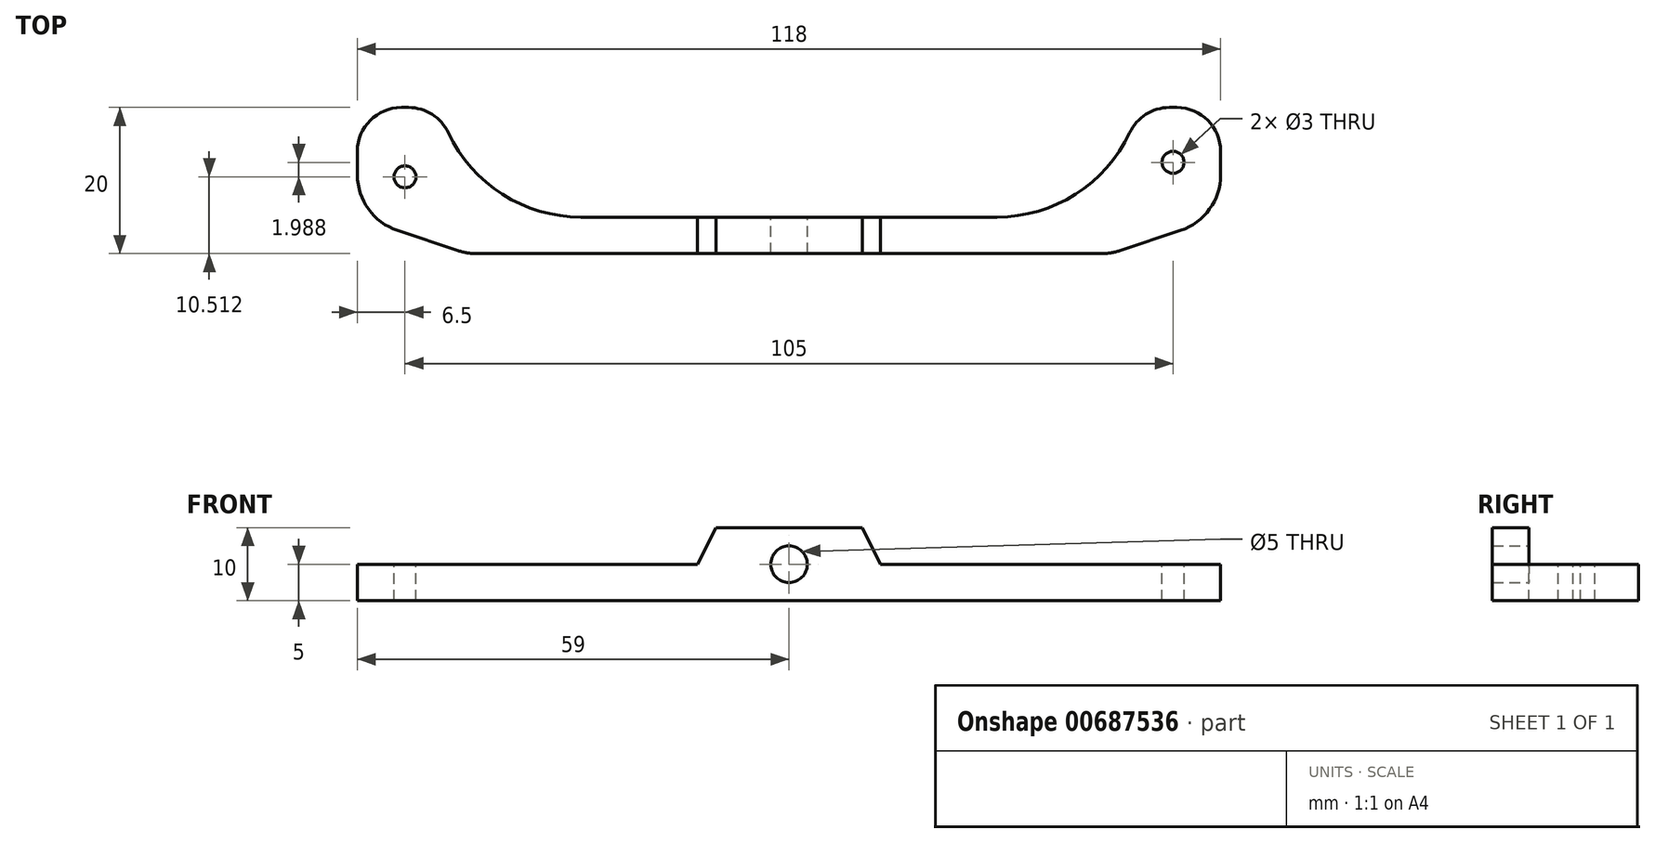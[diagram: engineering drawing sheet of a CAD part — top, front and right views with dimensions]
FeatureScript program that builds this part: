
annotation { "Feature Type Name" : "Feature", "Feature Type Description" : "" }
export const myFeature = defineFeature(function(context is Context, id is Id, definition is map)
    precondition{}
    {
        {
            var Q0;
            Q0=qCreatedBy(makeId("Top.planeOp"),FACE);
            var sketch = newSketch(context, id + "F0", { "sketchPlane" : qUnion([Q0])});
            skLineSegment(sketch, "E0", {"start": v(0, 0) * mm, "end": v(59, 0) * mm});
            skLineSegment(sketch, "E1", {"start": v(59, 0) * mm, "end": v(59, 20) * mm});
            skLineSegment(sketch, "E2", {"start": v(59, 20) * mm, "end": v(46, 20) * mm});
            skLineSegment(sketch, "E3", {"start": v(46, 20) * mm, "end": v(46, 5) * mm});
            skLineSegment(sketch, "E4", {"start": v(46, 5) * mm, "end": v(0, 5) * mm});
            skLineSegment(sketch, "E5", {"start": v(0, 5) * mm, "end": v(0, 0) * mm});
            skLineSegment(sketch, "E6.MirrorCS", {"start": v(-59, 20) * mm, "end": v(-46, 20) * mm});
            skLineSegment(sketch, "E7.MirrorCS", {"start": v(-46, 20) * mm, "end": v(-46, 5) * mm});
            skLineSegment(sketch, "E8.MirrorCS", {"start": v(-59, 0) * mm, "end": v(-59, 20) * mm});
            skLineSegment(sketch, "E9.MirrorCS", {"start": v(-46, 5) * mm, "end": v(0, 5) * mm});
            skLineSegment(sketch, "E10.MirrorCS", {"start": v(0, 0) * mm, "end": v(-59, 0) * mm});
            skSolve(sketch);
        }
        {
            var Q0;
            Q0=makeQuery(id+"F0.imprint","IMPRINT",FACE,{"disambiguationData":[TD([[makeQuery(id+"F0.imprint","IMPRINT",EDGE,{"derivedFrom":sQuery(id+"F0.wireOp",EDGE,"E5")}),-1.0]])]});
            var Q1;
            Q1=makeQuery(id+"F0.imprint","IMPRINT",FACE,{"disambiguationData":[TD([[makeQuery(id+"F0.imprint","IMPRINT",EDGE,{"derivedFrom":sQuery(id+"F0.wireOp",EDGE,"E0")}),1.0]])]});
            extrude(context, id + "F1", {"entities" : qUnion([Q0, Q1]), "depth" : 5 * mm, "offsetDistance" : 25 * mm});
        }
        {
            var Q0;
            Q0=qCreatedBy(makeId("Front.planeOp"),FACE);
            var sketch = newSketch(context, id + "F2", { "sketchPlane" : qUnion([Q0])});
            skLineSegment(sketch, "E11", {"start": v(0, 0) * mm, "end": v(0, 10) * mm});
            skLineSegment(sketch, "E12", {"start": v(0, 10) * mm, "end": v(-10, 10) * mm});
            skLineSegment(sketch, "E13", {"start": v(-10, 10) * mm, "end": v(-15, 0) * mm});
            skLineSegment(sketch, "E14", {"start": v(-15, 0) * mm, "end": v(0, 0) * mm});
            skLineSegment(sketch, "E15.MirrorCS", {"start": v(0, 10) * mm, "end": v(10, 10) * mm});
            skLineSegment(sketch, "E16.MirrorCS", {"start": v(10, 10) * mm, "end": v(15, 0) * mm});
            skLineSegment(sketch, "E17.MirrorCS", {"start": v(15, 0) * mm, "end": v(0, 0) * mm});
            skSolve(sketch);
        }
        {
            var Q0;
            Q0=makeQuery(id+"F2.imprint","IMPRINT",FACE,{"disambiguationData":[TD([[makeQuery(id+"F2.imprint","IMPRINT",EDGE,{"derivedFrom":sQuery(id+"F2.wireOp",EDGE,"E11")}),-1.0]])]});
            var Q1;
            Q1=makeQuery(id+"F2.imprint","IMPRINT",FACE,{"disambiguationData":[TD([[makeQuery(id+"F2.imprint","IMPRINT",EDGE,{"derivedFrom":sQuery(id+"F2.wireOp",EDGE,"E11")}),1.0]])]});
            extrude(context, id + "F3", {"entities" : qUnion([Q0, Q1]), "operationType" : NewBodyOperationType.ADD, "oppositeDirection" : true, "depth" : 5 * mm, "offsetDistance" : 25 * mm});
        }
        {
            var Q0;
            Q0=makeQuery(id+"F3.boolean.opBoolean","MERGE",FACE,{"derivedFrom":[makeQuery(id+"F1.opExtrude","SWEPT_FACE",FACE,{"disambiguationData":[OSD([sQuery(id+"F0.wireOp",EDGE,"E4"),sQuery(id+"F0.wireOp",EDGE,"E9.MirrorCS")])]}),makeQuery(id+"F3.opExtrude","CAP_FACE",FACE,{"disambiguationData":[OSD([sQuery(id+"F2.wireOp",EDGE,"E12"),sQuery(id+"F2.wireOp",EDGE,"E13"),sQuery(id+"F2.wireOp",EDGE,"E14"),sQuery(id+"F2.wireOp",EDGE,"E15.MirrorCS"),sQuery(id+"F2.wireOp",EDGE,"E16.MirrorCS"),sQuery(id+"F2.wireOp",EDGE,"E17.MirrorCS")])],"isStart":false})]});
            var sketch = newSketch(context, id + "F4", { "sketchPlane" : qUnion([Q0])});
            skCircle(sketch, "E18", {"center": v(0, 5) * mm, "radius": 2.5 * mm});
            skSolve(sketch);
        }
        {
            var Q0;
            Q0=makeQuery(id+"F4.imprint","IMPRINT",FACE,{"disambiguationData":[TD([[makeQuery(id+"F4.imprint","IMPRINT",EDGE,{"derivedFrom":sQuery(id+"F4.wireOp",EDGE,"E18")}),1.0]])]});
            extrude(context, id + "F5", {"entities" : qUnion([Q0]), "operationType" : NewBodyOperationType.REMOVE, "oppositeDirection" : true, "depth" : 25 * mm, "offsetDistance" : 25 * mm});
        }
        {
            var Q0;
            Q0=makeQuery(id+"F1.opExtrude","SWEPT_EDGE",EDGE,{"disambiguationData":[OSD([sQuery(id+"F0.wireOp",EDGE,"E1"),sQuery(id+"F0.wireOp",EDGE,"E2")])]});
            var Q1;
            Q1=makeQuery(id+"F1.opExtrude","SWEPT_EDGE",EDGE,{"disambiguationData":[OSD([sQuery(id+"F0.wireOp",EDGE,"E2"),sQuery(id+"F0.wireOp",EDGE,"E3")])]});
            var Q2;
            Q2=makeQuery(id+"F1.opExtrude","SWEPT_EDGE",EDGE,{"disambiguationData":[OSD([sQuery(id+"F0.wireOp",EDGE,"E6.MirrorCS"),sQuery(id+"F0.wireOp",EDGE,"E7.MirrorCS")])]});
            var Q3;
            Q3=makeQuery(id+"F1.opExtrude","SWEPT_EDGE",EDGE,{"disambiguationData":[OSD([sQuery(id+"F0.wireOp",EDGE,"E6.MirrorCS"),sQuery(id+"F0.wireOp",EDGE,"E8.MirrorCS")])]});
            fillet(context, id + "F6", {"entities" : qUnion([Q0, Q1, Q2, Q3]), "radius" : 6 * mm, "tangentPropagation" : true, "allowEdgeOverflow" : false});
        }
        {
            var Q0;
            {var subQ0=sQuery(id+"F0.wireOp",EDGE,"E3");var subQ1=sQuery(id+"F0.wireOp",EDGE,"E2");var subQ2=sQuery(id+"F0.wireOp",EDGE,"E1");var subQ3=sQuery(id+"F0.wireOp",EDGE,"E10.MirrorCS");var subQ4=sQuery(id+"F0.wireOp",EDGE,"E0");var subQ11=sQuery(id+"F0.wireOp",EDGE,"E9.MirrorCS");var subQ12=sQuery(id+"F0.wireOp",EDGE,"E4");Q0=makeQuery(id+"F3.boolean.opBoolean","SPLIT",FACE,{"disambiguationData":[TD([makeQuery(id+"F1.opExtrude","SWEPT_FACE",FACE,{"disambiguationData":[OSD([subQ2])]})])],"derivedFrom":makeQuery(id+"F1.opExtrude","CAP_FACE",FACE,{"disambiguationData":[OSD([subQ4,subQ2,subQ1,subQ0,subQ12,sQuery(id+"F0.wireOp",EDGE,"E6.MirrorCS"),sQuery(id+"F0.wireOp",EDGE,"E7.MirrorCS"),sQuery(id+"F0.wireOp",EDGE,"E8.MirrorCS"),subQ11,subQ3])],"isStart":false})});}
            var sketch = newSketch(context, id + "F7", { "sketchPlane" : qUnion([Q0])});
            skCircle(sketch, "E19", {"center": v(52.5, 12.5) * mm, "radius": 1.5 * mm});
            skCircle(sketch, "E20", {"center": v(-52.5, 10.51) * mm, "radius": 1.5 * mm});
            skSolve(sketch);
        }
        {
            var Q0;
            Q0=makeQuery(id+"F7.imprint","IMPRINT",FACE,{"disambiguationData":[TD([[makeQuery(id+"F7.imprint","IMPRINT",EDGE,{"derivedFrom":sQuery(id+"F7.wireOp",EDGE,"E19")}),1.0]])]});
            var Q1;
            Q1=makeQuery(id+"F7.imprint","IMPRINT",FACE,{"disambiguationData":[TD([[makeQuery(id+"F7.imprint","IMPRINT",EDGE,{"derivedFrom":sQuery(id+"F7.wireOp",EDGE,"E20")}),1.0]])]});
            extrude(context, id + "F8", {"entities" : qUnion([Q0, Q1]), "operationType" : NewBodyOperationType.REMOVE, "oppositeDirection" : true, "depth" : 25 * mm, "offsetDistance" : 25 * mm});
        }
        {
            var Q0;
            Q0=makeQuery(id+"F1.opExtrude","SWEPT_EDGE",EDGE,{"disambiguationData":[OSD([sQuery(id+"F0.wireOp",EDGE,"E3"),sQuery(id+"F0.wireOp",EDGE,"E4")])]});
            var Q1;
            Q1=makeQuery(id+"F1.opExtrude","SWEPT_EDGE",EDGE,{"disambiguationData":[OSD([sQuery(id+"F0.wireOp",EDGE,"E7.MirrorCS"),sQuery(id+"F0.wireOp",EDGE,"E9.MirrorCS")])]});
            fillet(context, id + "F9", {"entities" : qUnion([Q0, Q1]), "radius" : 20 * mm, "tangentPropagation" : true, "allowEdgeOverflow" : false});
        }
        {
            var Q0;
            Q0=makeQuery(id+"F1.opExtrude","SWEPT_EDGE",EDGE,{"disambiguationData":[OSD([sQuery(id+"F0.wireOp",EDGE,"E0"),sQuery(id+"F0.wireOp",EDGE,"E1")])]});
            var Q1;
            Q1=makeQuery(id+"F1.opExtrude","SWEPT_EDGE",EDGE,{"disambiguationData":[OSD([sQuery(id+"F0.wireOp",EDGE,"E8.MirrorCS"),sQuery(id+"F0.wireOp",EDGE,"E10.MirrorCS")])]});
            chamfer(context, id + "F10", {"entities" : qUnion([Q0, Q1]), "chamferType" : ChamferType.TWO_OFFSETS, "width1" : 5 * mm, "oppositeDirection" : false, "width2" : 15 * mm, "tangentPropagation" : true});
        }
        {
            var Q0;
            {var subQ0=sQuery(id+"F0.wireOp",EDGE,"E1");Q0=makeQuery(id+"F10.opChamfer","BLEND_EDGE",EDGE,{"blendedFrom":[makeQuery(id+"F1.opExtrude","SWEPT_EDGE",EDGE,{"disambiguationData":[OSD([sQuery(id+"F0.wireOp",EDGE,"E0"),subQ0])]}),makeQuery(id+"F1.opExtrude","SWEPT_FACE",FACE,{"disambiguationData":[OSD([subQ0])]})],"blendedInto":[makeQuery(id+"F1.opExtrude","SWEPT_FACE",FACE,{"disambiguationData":[OSD([subQ0])]})]});}
            var Q1;
            {var subQ0=sQuery(id+"F0.wireOp",EDGE,"E0");Q1=makeQuery(id+"F10.opChamfer","BLEND_EDGE",EDGE,{"blendedFrom":[makeQuery(id+"F1.opExtrude","SWEPT_EDGE",EDGE,{"disambiguationData":[OSD([subQ0,sQuery(id+"F0.wireOp",EDGE,"E1")])]}),makeQuery(id+"F3.boolean.opBoolean","MERGE",FACE,{"derivedFrom":[makeQuery(id+"F1.opExtrude","SWEPT_FACE",FACE,{"disambiguationData":[OSD([subQ0,sQuery(id+"F0.wireOp",EDGE,"E10.MirrorCS")])]}),makeQuery(id+"F3.opExtrude","CAP_FACE",FACE,{"disambiguationData":[OSD([sQuery(id+"F2.wireOp",EDGE,"E12"),sQuery(id+"F2.wireOp",EDGE,"E13"),sQuery(id+"F2.wireOp",EDGE,"E14"),sQuery(id+"F2.wireOp",EDGE,"E15.MirrorCS"),sQuery(id+"F2.wireOp",EDGE,"E16.MirrorCS"),sQuery(id+"F2.wireOp",EDGE,"E17.MirrorCS")])],"isStart":true})]})],"blendedInto":[makeQuery(id+"F3.boolean.opBoolean","MERGE",FACE,{"derivedFrom":[makeQuery(id+"F1.opExtrude","SWEPT_FACE",FACE,{"disambiguationData":[OSD([subQ0,sQuery(id+"F0.wireOp",EDGE,"E10.MirrorCS")])]}),makeQuery(id+"F3.opExtrude","CAP_FACE",FACE,{"disambiguationData":[OSD([sQuery(id+"F2.wireOp",EDGE,"E12"),sQuery(id+"F2.wireOp",EDGE,"E13"),sQuery(id+"F2.wireOp",EDGE,"E14"),sQuery(id+"F2.wireOp",EDGE,"E15.MirrorCS"),sQuery(id+"F2.wireOp",EDGE,"E16.MirrorCS"),sQuery(id+"F2.wireOp",EDGE,"E17.MirrorCS")])],"isStart":true})]})]});}
            var Q2;
            {var subQ0=sQuery(id+"F0.wireOp",EDGE,"E10.MirrorCS");Q2=makeQuery(id+"F10.opChamfer","BLEND_EDGE",EDGE,{"blendedFrom":[makeQuery(id+"F1.opExtrude","SWEPT_EDGE",EDGE,{"disambiguationData":[OSD([sQuery(id+"F0.wireOp",EDGE,"E8.MirrorCS"),subQ0])]}),makeQuery(id+"F3.boolean.opBoolean","MERGE",FACE,{"derivedFrom":[makeQuery(id+"F1.opExtrude","SWEPT_FACE",FACE,{"disambiguationData":[OSD([sQuery(id+"F0.wireOp",EDGE,"E0"),subQ0])]}),makeQuery(id+"F3.opExtrude","CAP_FACE",FACE,{"disambiguationData":[OSD([sQuery(id+"F2.wireOp",EDGE,"E12"),sQuery(id+"F2.wireOp",EDGE,"E13"),sQuery(id+"F2.wireOp",EDGE,"E14"),sQuery(id+"F2.wireOp",EDGE,"E15.MirrorCS"),sQuery(id+"F2.wireOp",EDGE,"E16.MirrorCS"),sQuery(id+"F2.wireOp",EDGE,"E17.MirrorCS")])],"isStart":true})]})],"blendedInto":[makeQuery(id+"F3.boolean.opBoolean","MERGE",FACE,{"derivedFrom":[makeQuery(id+"F1.opExtrude","SWEPT_FACE",FACE,{"disambiguationData":[OSD([sQuery(id+"F0.wireOp",EDGE,"E0"),subQ0])]}),makeQuery(id+"F3.opExtrude","CAP_FACE",FACE,{"disambiguationData":[OSD([sQuery(id+"F2.wireOp",EDGE,"E12"),sQuery(id+"F2.wireOp",EDGE,"E13"),sQuery(id+"F2.wireOp",EDGE,"E14"),sQuery(id+"F2.wireOp",EDGE,"E15.MirrorCS"),sQuery(id+"F2.wireOp",EDGE,"E16.MirrorCS"),sQuery(id+"F2.wireOp",EDGE,"E17.MirrorCS")])],"isStart":true})]})]});}
            var Q3;
            {var subQ0=sQuery(id+"F0.wireOp",EDGE,"E8.MirrorCS");Q3=makeQuery(id+"F10.opChamfer","BLEND_EDGE",EDGE,{"blendedFrom":[makeQuery(id+"F1.opExtrude","SWEPT_EDGE",EDGE,{"disambiguationData":[OSD([subQ0,sQuery(id+"F0.wireOp",EDGE,"E10.MirrorCS")])]}),makeQuery(id+"F1.opExtrude","SWEPT_FACE",FACE,{"disambiguationData":[OSD([subQ0])]})],"blendedInto":[makeQuery(id+"F1.opExtrude","SWEPT_FACE",FACE,{"disambiguationData":[OSD([subQ0])]})]});}
            fillet(context, id + "F11", {"entities" : qUnion([Q0, Q1, Q2, Q3]), "radius" : 8 * mm, "tangentPropagation" : true, "allowEdgeOverflow" : false});
        }
    });
